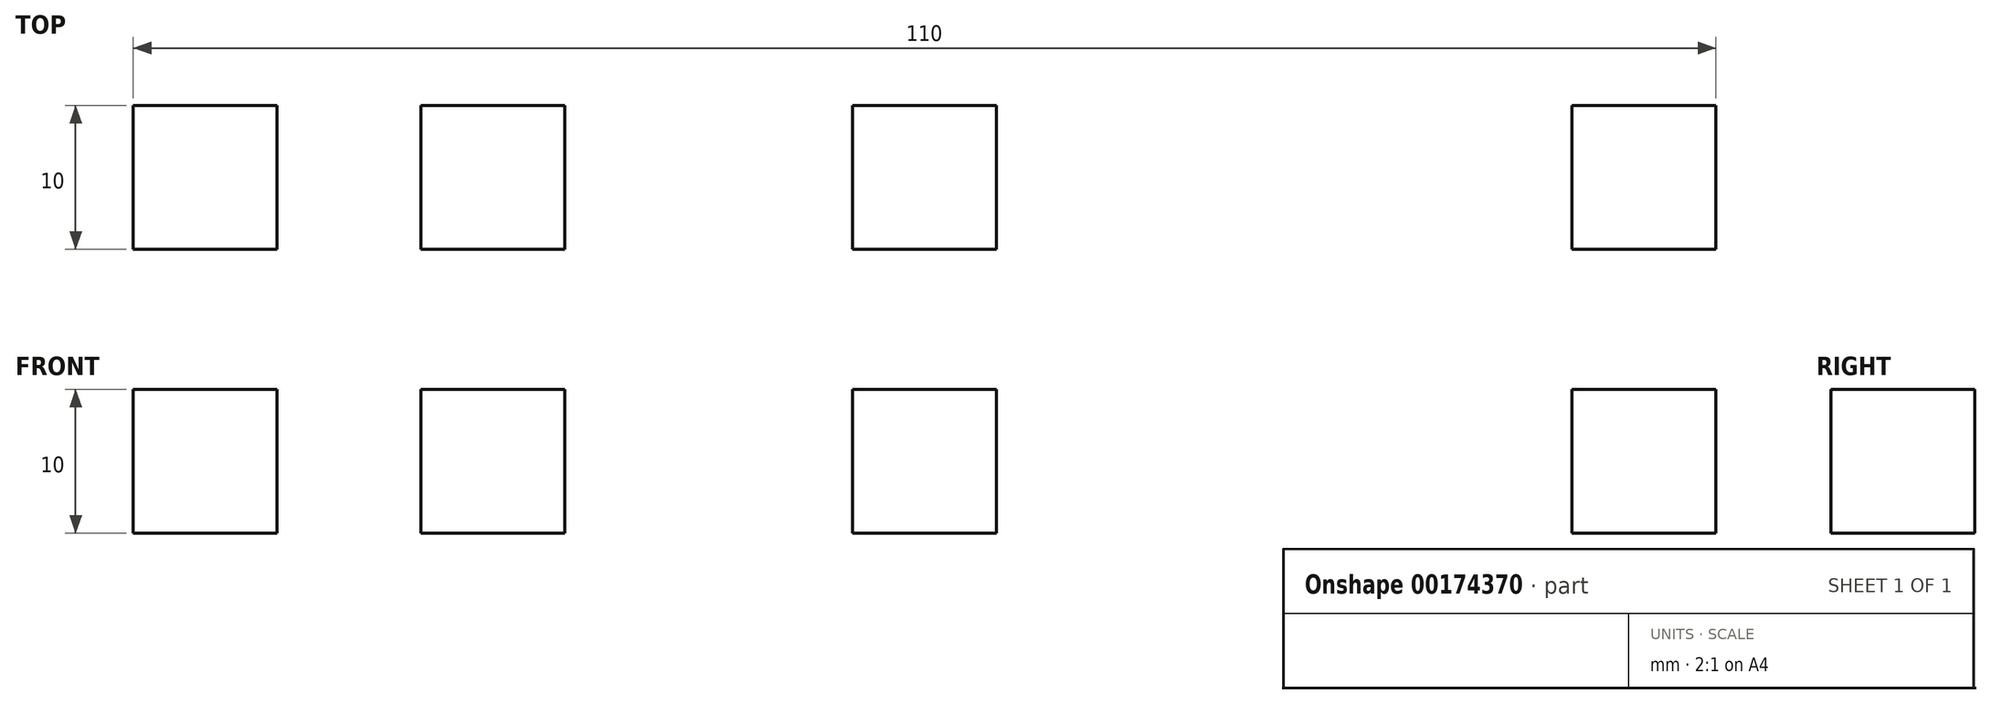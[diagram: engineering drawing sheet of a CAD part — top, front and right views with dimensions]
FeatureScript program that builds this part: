
annotation { "Feature Type Name" : "Feature", "Feature Type Description" : "" }
export const myFeature = defineFeature(function(context is Context, id is Id, definition is map)
    precondition{}
    {
        {
            var Q0;
            Q0=qCreatedBy(makeId("Top.planeOp"),FACE);
            var sketch = newSketch(context, id + "F0", { "sketchPlane" : qUnion([Q0])});
            skLineSegment(sketch, "E0.bottom", {"start": v(5, 5) * mm, "end": v(-5, 5) * mm});
            skLineSegment(sketch, "E0.top", {"start": v(5, -5) * mm, "end": v(-5, -5) * mm});
            skLineSegment(sketch, "E0.left", {"start": v(5, 5) * mm, "end": v(5, -5) * mm});
            skLineSegment(sketch, "E0.right", {"start": v(-5, 5) * mm, "end": v(-5, -5) * mm});
            skPoint(sketch, "E0.middle", {"position": v(0, 0) * mm});
            skLineSegment(sketch, "E1.bottom", {"start": v(15, 5) * mm, "end": v(25, 5) * mm});
            skLineSegment(sketch, "E1.top", {"start": v(15, -5) * mm, "end": v(25, -5) * mm});
            skLineSegment(sketch, "E1.left", {"start": v(15, 5) * mm, "end": v(15, -5) * mm});
            skLineSegment(sketch, "E1.right", {"start": v(25, 5) * mm, "end": v(25, -5) * mm});
            skPoint(sketch, "E1.middle", {"position": v(20, 0) * mm});
            skLineSegment(sketch, "E2.bottom", {"start": v(55, 5) * mm, "end": v(45, 5) * mm});
            skLineSegment(sketch, "E2.top", {"start": v(55, -5) * mm, "end": v(45, -5) * mm});
            skLineSegment(sketch, "E2.left", {"start": v(55, 5) * mm, "end": v(55, -5) * mm});
            skLineSegment(sketch, "E2.right", {"start": v(45, 5) * mm, "end": v(45, -5) * mm});
            skPoint(sketch, "E2.middle", {"position": v(50, 0) * mm});
            skLineSegment(sketch, "E3.bottom", {"start": v(105, 5) * mm, "end": v(95, 5) * mm});
            skLineSegment(sketch, "E3.top", {"start": v(105, -5) * mm, "end": v(95, -5) * mm});
            skLineSegment(sketch, "E3.left", {"start": v(105, 5) * mm, "end": v(105, -5) * mm});
            skLineSegment(sketch, "E3.right", {"start": v(95, 5) * mm, "end": v(95, -5) * mm});
            skPoint(sketch, "E3.middle", {"position": v(100, 0) * mm});
            skSolve(sketch);
        }
        {
            var Q0;
            Q0=makeQuery(id+"F0.imprint","IMPRINT",FACE,{"disambiguationData":[TD([[makeQuery(id+"F0.imprint","IMPRINT",EDGE,{"derivedFrom":sQuery(id+"F0.wireOp",EDGE,"E1.bottom")}),-1.0]])]});
            var Q1;
            Q1=makeQuery(id+"F0.imprint","IMPRINT",FACE,{"disambiguationData":[TD([[makeQuery(id+"F0.imprint","IMPRINT",EDGE,{"derivedFrom":sQuery(id+"F0.wireOp",EDGE,"E0.bottom")}),1.0]])]});
            var Q2;
            Q2=makeQuery(id+"F0.imprint","IMPRINT",FACE,{"disambiguationData":[TD([[makeQuery(id+"F0.imprint","IMPRINT",EDGE,{"derivedFrom":sQuery(id+"F0.wireOp",EDGE,"E2.bottom")}),1.0]])]});
            var Q3;
            Q3=makeQuery(id+"F0.imprint","IMPRINT",FACE,{"disambiguationData":[TD([[makeQuery(id+"F0.imprint","IMPRINT",EDGE,{"derivedFrom":sQuery(id+"F0.wireOp",EDGE,"E3.bottom")}),1.0]])]});
            extrude(context, id + "F1", {"entities" : qUnion([Q0, Q1, Q2, Q3]), "depth" : 10 * mm});
        }
    });
